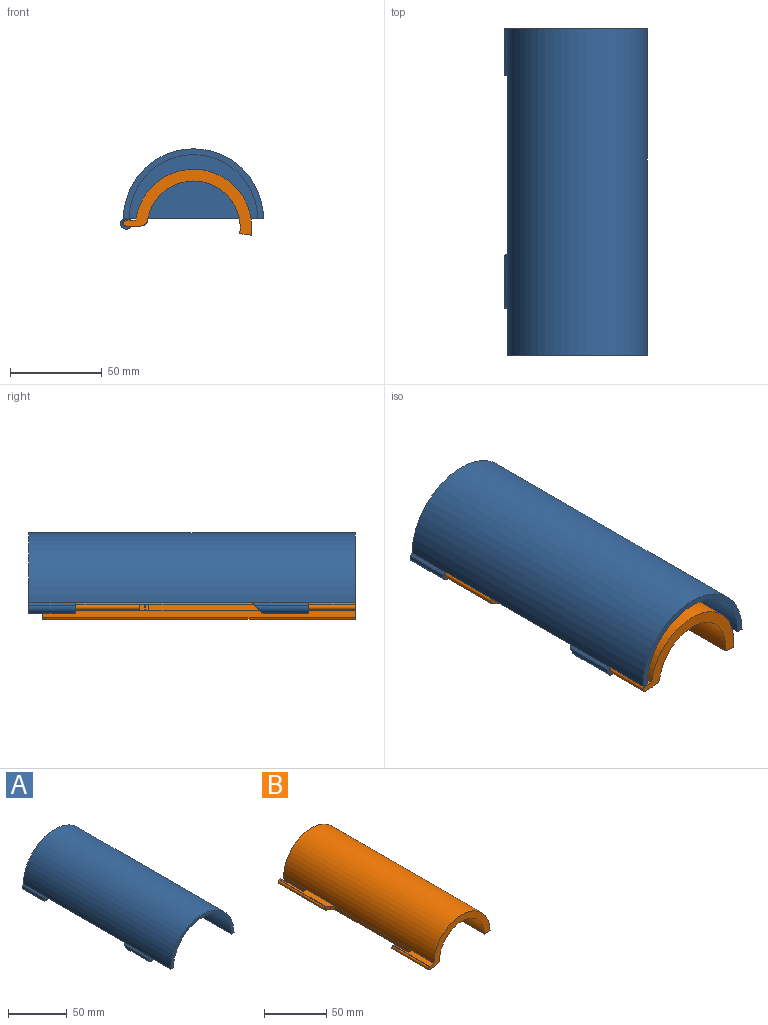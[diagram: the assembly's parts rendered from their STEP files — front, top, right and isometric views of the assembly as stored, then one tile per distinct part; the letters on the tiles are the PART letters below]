
ASSEMBLY  parts=2 mates=1
PART A: 20 faces, bbox 78.3x178.3x44.2 mm
  f0: plane 76.2x38.1mm, normal (0,-1,0), area 364.2mm2, adj f8,f9,f10,f13
  f1: extruded ~30.48x1.37mm, area 56.5mm2, adj f3,f10,f14,f19
  f2: extruded ~25.4x1.37mm, area 48.2mm2, adj f4,f10,f11,f16
  f3: cylinder r=3.17mm len=29.2mm, axis (0,-1,0), area 329.3mm2, adj f1,f5,f14,f17,f19
  f4: cylinder r=3.17mm len=25.4mm, axis (0,-1,0), area 312.8mm2, adj f2,f6,f11,f16
  f5: extruded ~30.48x1.37mm, area 56.6mm2, adj f3,f9,f14,f19
  f6: extruded ~25.4x1.37mm, area 48.3mm2, adj f4,f8,f9,f11,f16
  f7: cylinder r=1.91mm len=25.4mm, axis (0,-1,0), area 304mm2, adj f11,f16
  f8: plane 177.8x73.03mm, normal (0,0,-1), area 1008.1mm2, adj f0,f6,f9,f10,f11,f12
  f9: cylinder r=34.92mm len=171.45mm, axis (0,1,0), area 18811.5mm2, adj f0,f5,f6,f8,f12,f13,f15
  f10: cylinder r=38.1mm len=177.8mm, axis (0,1,0), area 21281.7mm2, adj f0,f1,f2,f8,f11,f13,f15
  f11: plane 77.79x43.69mm, normal (0,1,0), area 2297.5mm2, adj f2,f4,f6,f7,f8,f10
  f12: plane 69.85x34.93mm, normal (0,-1,0), area 1916mm2, adj f8,f9
  f13: plane 25.4x3.18mm, normal (0,0,-1), area 80.6mm2, adj f0,f9,f10,f14
  f14: plane 6.35x5.59mm, normal (0,-1,0), area 17.4mm2, adj f1,f3,f5,f13,f18
  f15: plane 96.52x3.18mm, normal (0,0,-1), area 306.5mm2, adj f9,f10,f16,f19
  f16: plane 6.35x5.59mm, normal (0,-1,0), area 17.4mm2, adj f2,f4,f6,f7,f15
  f17: plane 3.47x0.51mm, normal (0,1,0), area 1.2mm2, adj f3,f19
  f18: cylinder r=1.91mm len=29.99mm, axis (0,-1,0), area 335.9mm2, adj f14,f19
  f19: plane 6.83x5.56mm, normal (0,0.71,-0.71), area 22.8mm2, adj f1,f3,f5,f15,f17,f18
PART B: 26 faces, bbox 69.9x170.2x35.8 mm
  f0: extruded ~170.18x10.79mm, area 1623.6mm2, adj f5,f6,f7,f10,f11,f12,f15,f16
  f1: extruded ~57.89x4.78mm, area 187.5mm2, adj f7,f9,f13,f16,f17,f21,f24,f25
  f2: extruded ~41.22x4.77mm, area 148.9mm2, adj f3,f6,f9,f11,f19,f23
  f3: extruded ~41.22x0.44mm, area 18.2mm2, adj f2,f4,f11,f23
  f4: cylinder r=1.59mm len=41.22mm, axis (0,-1,0), area 192.3mm2, adj f3,f5,f11,f23
  f5: extruded ~41.22x0.28mm, area 11.6mm2, adj f0,f4,f11,f23
  f6: plane 15.86x3.19mm, normal (1,0,0), area 50.5mm2, adj f0,f2,f19,f23
  f7: plane 3.38x3.24mm, normal (0,1,0), area 9.2mm2, adj f0,f1,f13,f14,f15,f16
  f8: plane 170.18x6.35mm, normal (0,0,-1), area 1080.6mm2, adj f9,f10,f11,f12
  f9: cylinder r=31.75mm len=170.18mm, axis (0,1,0), area 16974.7mm2, adj f1,f2,f8,f11,f12,f18,f20
  f10: cylinder r=25.4mm len=170.18mm, axis (0,1,0), area 13579.8mm2, adj f0,f8,f11,f12
  f11: plane 69.89x35.73mm, normal (0,-1,0), area 606.2mm2, adj f0,f2,f3,f4,f5,f8,f9,f10
  f12: plane 63.76x35.52mm, normal (0,1,0), area 586.6mm2, adj f0,f8,f9,f10,f18
  f13: extruded ~53.11x0.44mm, area 23.4mm2, adj f1,f7,f14,f22,f25
  f14: cylinder r=1.59mm len=53.16mm, axis (0,-1,0), area 246.3mm2, adj f7,f13,f15,f22,f25
  f15: extruded ~53.44x0.28mm, area 14.9mm2, adj f0,f7,f14,f25
  f16: plane 25.4x3.19mm, normal (1,0,0), area 80.9mm2, adj f0,f1,f7,f17
  f17: plane 3.8x3.21mm, normal (0,1,0), area 10.4mm2, adj f0,f1,f16,f18
  f18: plane 25.42x3.52mm, normal (-1,0,0), area 88.9mm2, adj f0,f9,f12,f17
  f19: plane 3.8x3.21mm, normal (0,1,0), area 10.4mm2, adj f0,f2,f6,f20
  f20: plane 86.94x3.52mm, normal (-1,0,0), area 304.2mm2, adj f0,f9,f19,f24
  f21: plane 3.24x0.01mm, normal (-1,0,0), area 0mm2, adj f0,f1,f24,f25
  f22: plane 3.1x1.27mm, normal (0,-1,0), area 3mm2, adj f13,f14,f25
  f23: plane 3.38x3.24mm, normal (0,1,0), area 9.2mm2, adj f0,f2,f3,f4,f5,f6
  f24: plane 3.72x2.15mm, normal (-0.71,-0.71,0), area 10.1mm2, adj f0,f1,f20,f21
  f25: plane 3.52x2.99mm, normal (-0.71,-0.71,0), area 13.4mm2, adj f0,f1,f13,f14,f15,f21,f22
PLACE A t=(2.47,93,-80.92)mm fixed
PLACE B rot(axis=(0,1,0),7.4deg) t=(2.52,85.43,-85.7)mm
MATE revolute A.f3 <-> B.f4  axis (0,-1,0) through (-34.04,-59.4,-83.34)mm
